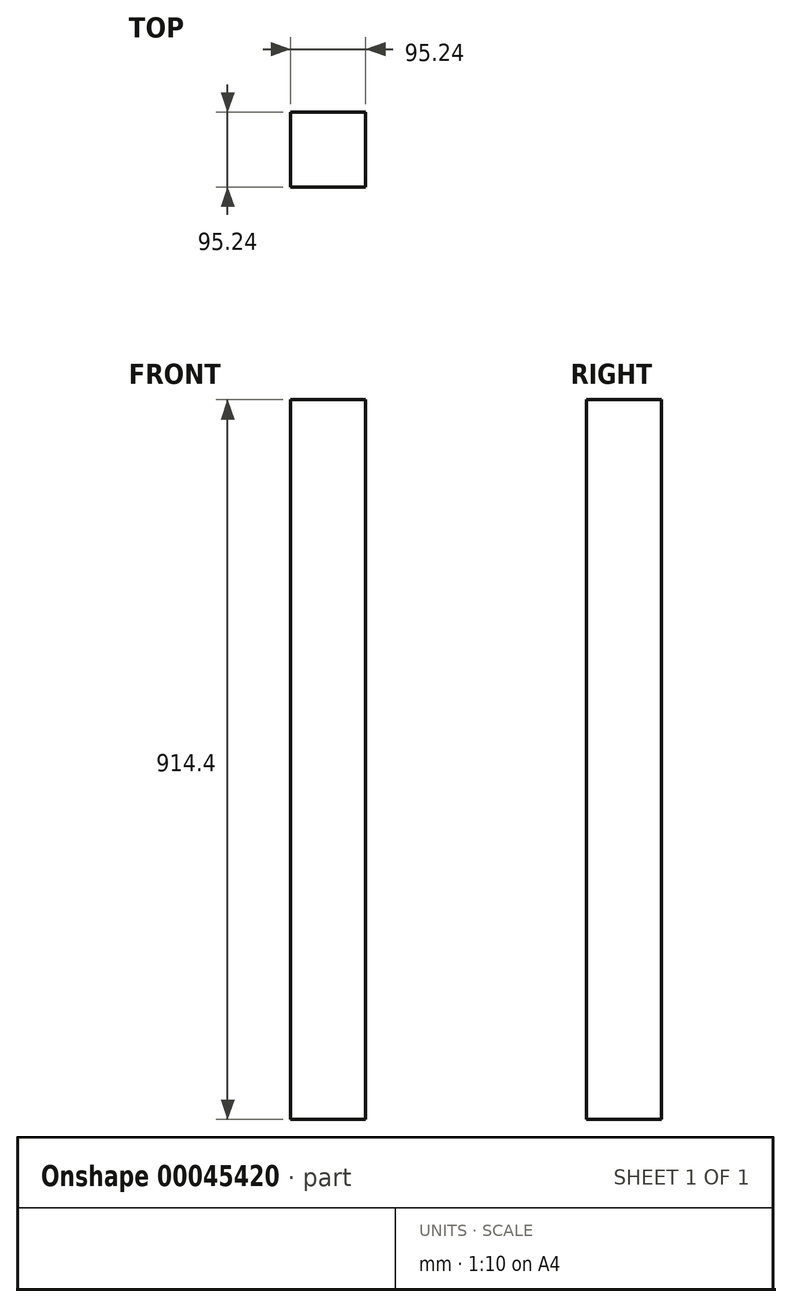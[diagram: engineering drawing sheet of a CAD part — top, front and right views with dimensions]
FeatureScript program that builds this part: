
annotation { "Feature Type Name" : "Feature", "Feature Type Description" : "" }
export const myFeature = defineFeature(function(context is Context, id is Id, definition is map)
    precondition{}
    {
        {
            var Q0;
            Q0=qCreatedBy(makeId("Top.planeOp"),FACE);
            var sketch = newSketch(context, id + "F0", { "sketchPlane" : qUnion([Q0])});
            skLineSegment(sketch, "E0.rect.bottom", {"start": v(47.63, -47.62) * mm, "end": v(-47.63, -47.63) * mm});
            skLineSegment(sketch, "E0.rect.top", {"start": v(47.63, 47.63) * mm, "end": v(-47.63, 47.63) * mm});
            skLineSegment(sketch, "E0.rect.left", {"start": v(47.63, -47.63) * mm, "end": v(47.63, 47.63) * mm});
            skLineSegment(sketch, "E0.rect.right", {"start": v(-47.63, -47.63) * mm, "end": v(-47.63, 47.63) * mm});
            skPoint(sketch, "E0.rect.middle", {"position": v(0, 0) * mm});
            skSolve(sketch);
        }
        {
            var Q0;
            Q0=makeQuery(id+"F0.imprint","IMPRINT",FACE,{"disambiguationData":[TD([[makeQuery(id+"F0.imprint","IMPRINT",EDGE,{"derivedFrom":sQuery(id+"F0.wireOp",EDGE,"E0.rect.bottom")}),-1.0]])]});
            extrude(context, id + "F1", {"entities" : qUnion([Q0]), "depth" : 914.4 * mm});
        }
    });
